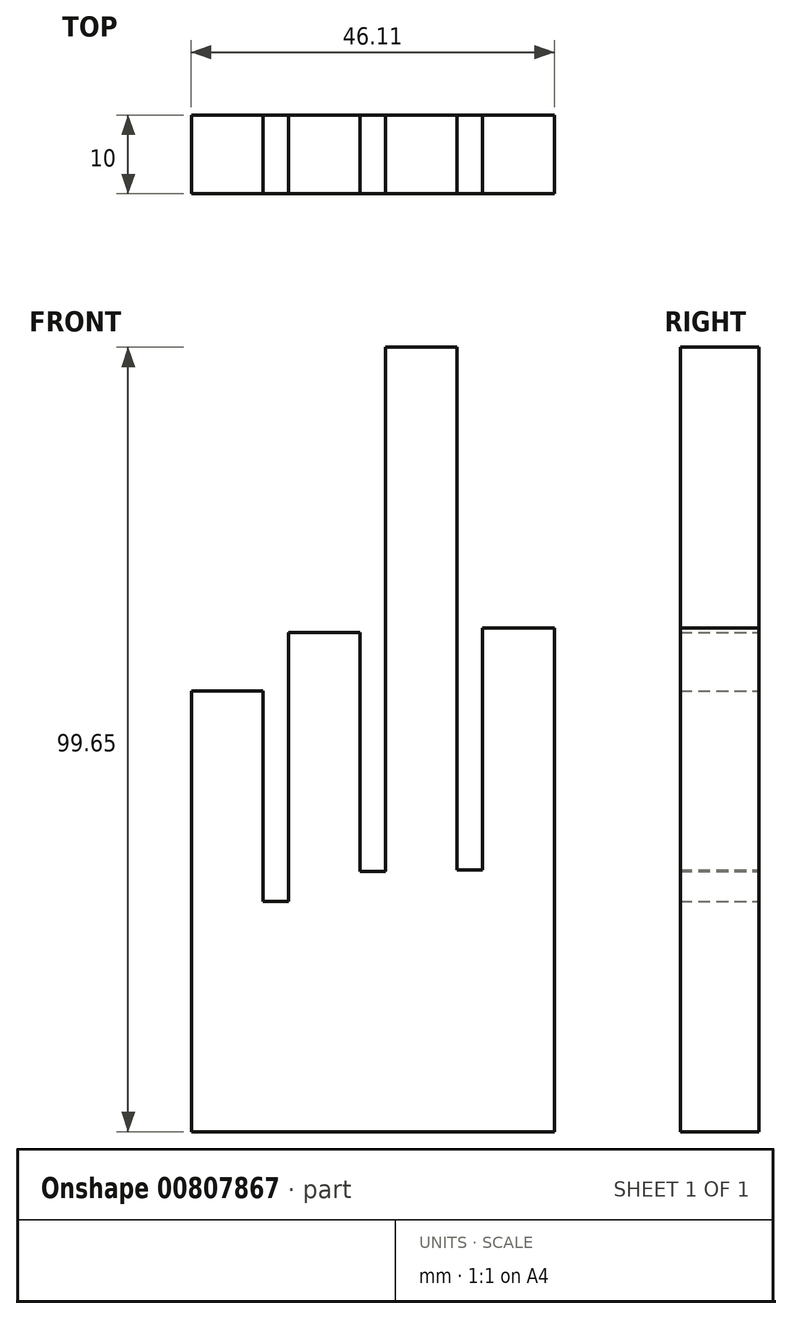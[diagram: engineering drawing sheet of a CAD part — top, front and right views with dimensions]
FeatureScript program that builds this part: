
annotation { "Feature Type Name" : "Feature", "Feature Type Description" : "" }
export const myFeature = defineFeature(function(context is Context, id is Id, definition is map)
    precondition{}
    {
        {
            var Q0;
            Q0=qCreatedBy(makeId("Front.planeOp"),FACE);
            var sketch = newSketch(context, id + "F0", { "sketchPlane" : qUnion([Q0])});
            skLineSegment(sketch, "E0", {"start": v(-45.64, -26.5) * mm, "end": v(-45.64, 29.5) * mm});
            skLineSegment(sketch, "E1", {"start": v(-45.64, 29.5) * mm, "end": v(-36.53, 29.5) * mm});
            skLineSegment(sketch, "E2", {"start": v(-36.53, 29.5) * mm, "end": v(-36.53, 2.75) * mm});
            skLineSegment(sketch, "E3", {"start": v(-36.53, 2.75) * mm, "end": v(-33.3, 2.75) * mm});
            skLineSegment(sketch, "E4", {"start": v(-33.3, 2.75) * mm, "end": v(-33.3, 36.9) * mm});
            skLineSegment(sketch, "E5", {"start": v(-33.3, 36.9) * mm, "end": v(-24.2, 36.9) * mm});
            skLineSegment(sketch, "E6", {"start": v(-24.2, 36.9) * mm, "end": v(-24.2, 6.55) * mm});
            skLineSegment(sketch, "E7", {"start": v(-24.2, 6.55) * mm, "end": v(-20.97, 6.55) * mm});
            skLineSegment(sketch, "E8", {"start": v(-20.97, 6.55) * mm, "end": v(-20.97, 73.15) * mm});
            skLineSegment(sketch, "E9", {"start": v(-20.97, 73.15) * mm, "end": v(-11.86, 73.15) * mm});
            skLineSegment(sketch, "E10", {"start": v(-11.86, 73.15) * mm, "end": v(-11.86, 6.74) * mm});
            skLineSegment(sketch, "E11", {"start": v(-11.86, 6.74) * mm, "end": v(-8.63, 6.74) * mm});
            skLineSegment(sketch, "E12", {"start": v(-8.63, 6.74) * mm, "end": v(-8.63, 37.48) * mm});
            skLineSegment(sketch, "E13", {"start": v(-8.63, 37.48) * mm, "end": v(0.47, 37.48) * mm});
            skLineSegment(sketch, "E14", {"start": v(0.47, 37.48) * mm, "end": v(0.47, -26.5) * mm});
            skLineSegment(sketch, "E15", {"start": v(0.47, -26.5) * mm, "end": v(-45.64, -26.5) * mm});
            skSolve(sketch);
        }
        {
            var Q0;
            Q0 = qSketchRegion(id + "F0", true);
            extrude(context, id + "F1", {"entities" : qUnion([Q0]), "depth" : 10 * mm, "offsetDistance" : 25 * mm});
        }
    });
